# Revit family: Leviton_CATSTD-LDC-66-W-D01
name_source: partatom
category: Electrical Equipment
units: mm (PartAtom-declared; Revit-internal decimal feet)

## family parameters
Always vertical = Yes
Cut with Voids When Loaded = Yes
Host = Wall
Maintain Annotation Orientation = No
Panel Configuration = Two Columns, Circuits Across
Part Type = Panelboard
Room Calculation Point = No
Round Connector Dimension = Use Diameter
Shared = No

## types (1)
- LDC66-W
    Cost = 1 $
    Default Elevation = 0 "
    Description = 66 Space Indoor Load Center Cover and Door with Window
    Dimensions = 57.803" H x 15.465" W x 0.917" D
    Ground Bus = No
    Manufacturer = Leviton
    Model = LDC66POS
    NEMA Enclosure Type = NEMA 1 Indoor
    Neutral Bus = No
    Neutral Rating = 0.00%
    Number of Pole = 1
    Overall Height = 57.803 "
    Overall Width = 15.465 "
    Product Data = https://www.arcat.com
    Specification = https://www.arcat.com
    URL = https://www.leviton.com
    Unit Depth = 0.917 "
    Unit Height = 55.889 "
    Unit Width = 14.116 "
    Voltage_MEP = 0 V
    Weight = 29.00 lbf

## geometry (parser evidence)
native form markers: Sweep x6
no freeform markers — native parametric forms only
